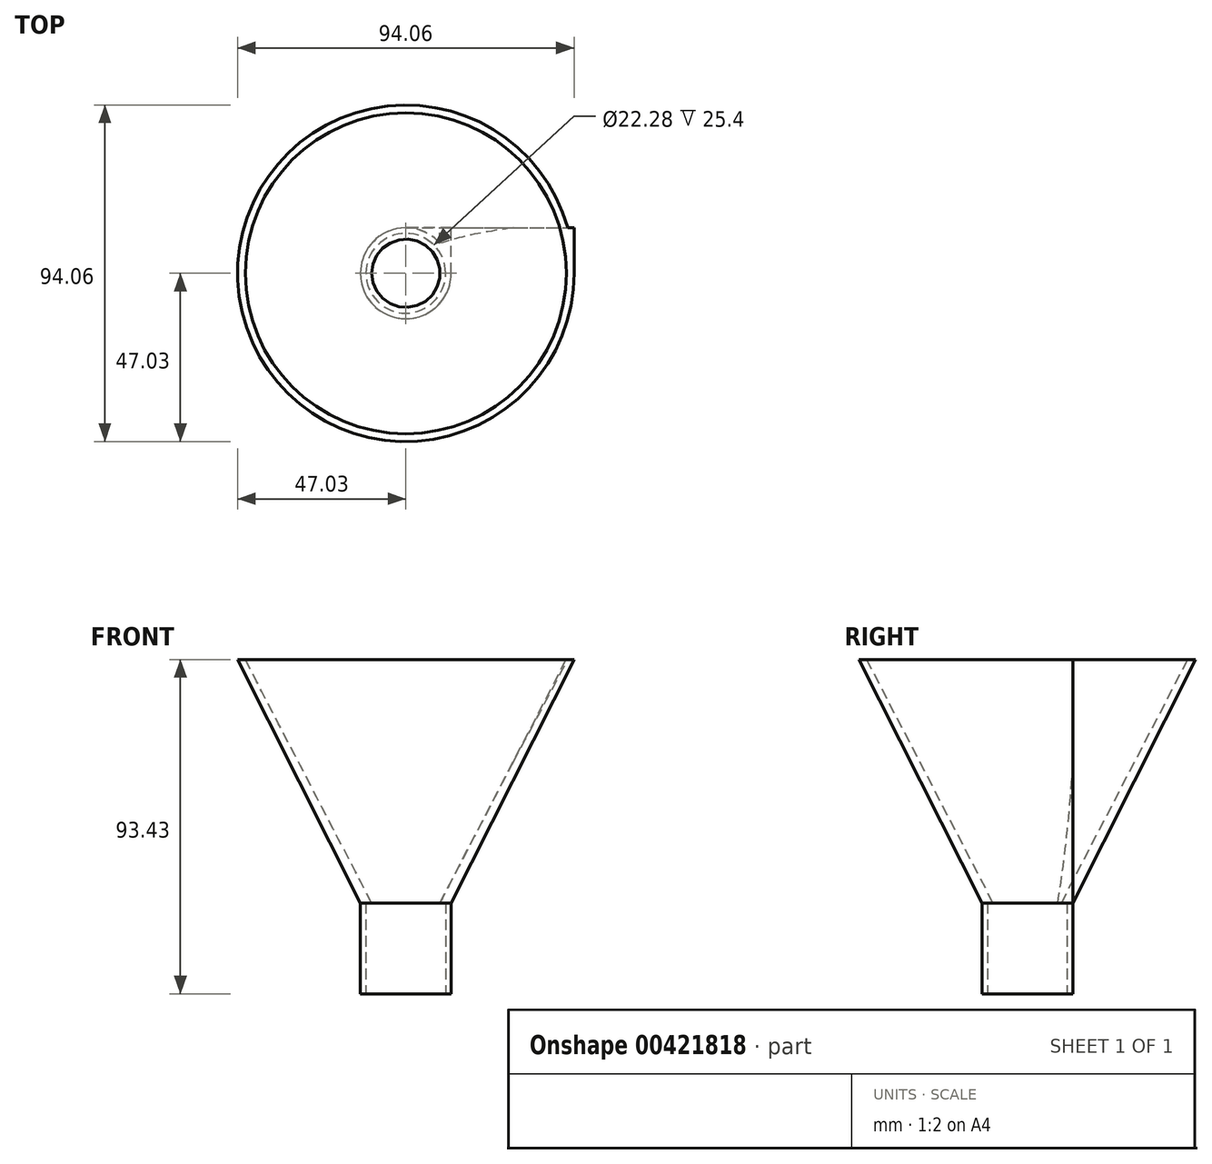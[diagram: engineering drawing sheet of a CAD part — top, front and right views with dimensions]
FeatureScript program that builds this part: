
annotation { "Feature Type Name" : "Feature", "Feature Type Description" : "" }
export const myFeature = defineFeature(function(context is Context, id is Id, definition is map)
    precondition{}
    {
        {
            var Q0;
            Q0=qCreatedBy(makeId("Front.planeOp"),FACE);
            var sketch = newSketch(context, id + "F0", { "sketchPlane" : qUnion([Q0])});
            skLineSegment(sketch, "E0", {"start": v(12.7, 5.54) * mm, "end": v(47.03, 73.57) * mm});
            skLineSegment(sketch, "E1", {"start": v(47.03, 73.57) * mm, "end": v(12.7, 5.54) * mm});
            skLineSegment(sketch, "E2", {"start": v(12.7, 5.54) * mm, "end": v(12.7, -19.86) * mm});
            skLineSegment(sketch, "E3", {"start": v(12.7, -19.86) * mm, "end": v(0, -19.86) * mm});
            skLineSegment(sketch, "E4", {"start": v(0, -19.86) * mm, "end": v(0, 5.54) * mm});
            skLineSegment(sketch, "E5", {"start": v(0, 5.54) * mm, "end": v(9.55, 5.54) * mm});
            skLineSegment(sketch, "E6", {"start": v(9.55, 5.54) * mm, "end": v(44.87, 73.57) * mm});
            skLineSegment(sketch, "E7", {"start": v(44.87, 73.57) * mm, "end": v(47.03, 73.57) * mm});
            skSolve(sketch);
        }
        {
            var Q0;
            Q0 = qSketchRegion(id + "F0", true);
            extrude(context, id + "F1", {"entities" : qUnion([Q0]), "depth" : 12.7 * mm});
        }
        {
            var Q0;
            Q0=makeQuery(id+"F1.opExtrude","CAP_FACE",FACE,{"disambiguationData":[OSD([sQuery(id+"F0.wireOp",EDGE,"E1"),sQuery(id+"F0.wireOp",EDGE,"E2"),sQuery(id+"F0.wireOp",EDGE,"E3"),sQuery(id+"F0.wireOp",EDGE,"E4"),sQuery(id+"F0.wireOp",EDGE,"E5"),sQuery(id+"F0.wireOp",EDGE,"E6"),sQuery(id+"F0.wireOp",EDGE,"E7")])],"isStart":false});
            var Q1;
            Q1=makeQuery(id+"F1.opExtrude","CAP_EDGE",EDGE,{"disambiguationData":[OSD([sQuery(id+"F0.wireOp",EDGE,"E4")])],"isStart":false});
            revolve(context, id + "F2", {"operationType" : NewBodyOperationType.ADD, "entities" : qUnion([Q0]), "axis" : qUnion([Q1]), "revolveType" : RevolveType.FULL});
        }
        {
            var Q0;
            {var subQ0=sQuery(id+"F0.wireOp",EDGE,"E3");Q0=makeQuery(id+"F2.boolean.opBoolean","MERGE",FACE,{"derivedFrom":[makeQuery(id+"F1.opExtrude","SWEPT_FACE",FACE,{"disambiguationData":[OSD([subQ0])]}),makeQuery(id+"F2.opRevolve","SWEPT_FACE",FACE,{"disambiguationData":[OSD([subQ0])]})]});}
            var sketch = newSketch(context, id + "F3", { "sketchPlane" : qUnion([Q0])});
            skCircle(sketch, "E8", {"center": v(0, 12.7) * mm, "radius": 11.14 * mm});
            skSolve(sketch);
        }
        {
            var Q0;
            Q0 = qSketchRegion(id + "F3", true);
            extrude(context, id + "F4", {"entities" : qUnion([Q0]), "operationType" : NewBodyOperationType.REMOVE, "oppositeDirection" : true, "depth" : 25.4 * mm});
        }
    });
